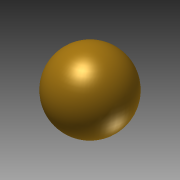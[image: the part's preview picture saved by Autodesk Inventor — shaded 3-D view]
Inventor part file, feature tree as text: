
AUTODESK INVENTOR PART (.ipt)
format: ipt  version: 2011 SP2 (Build 150309200, 309)  size: 98,304 bytes
history: native  units: mm
features: revolve x1, sketch x1
ambient origin geometry x8: Origin, YZ Plane, XZ Plane, XY Plane, X Axis, Y Axis, Z Axis, Center Point
bodies: Solid1 (feature_tree)
feature tree (2):
  revolve  "Revolution1"  Angle=90.0deg
  sketch  "Sketch1"  dims[d0=12.0mm d1=90.0deg]
